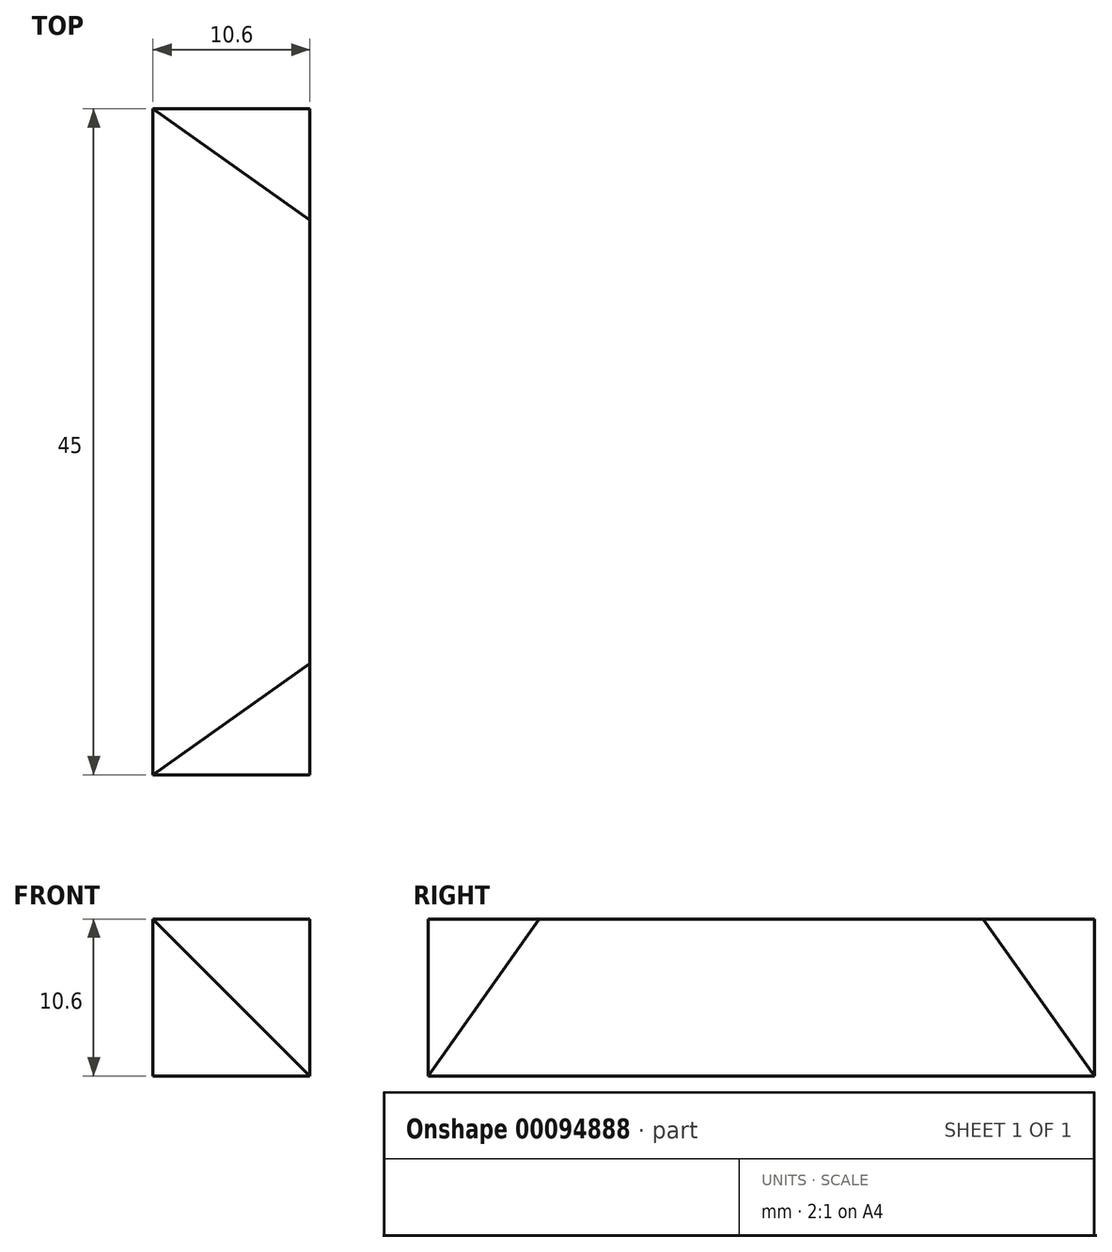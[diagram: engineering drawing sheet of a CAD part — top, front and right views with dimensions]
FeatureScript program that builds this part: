
annotation { "Feature Type Name" : "Feature", "Feature Type Description" : "" }
export const myFeature = defineFeature(function(context is Context, id is Id, definition is map)
    precondition{}
    {
        {
            var Q0;
            Q0=qCreatedBy(makeId("Front.planeOp"),FACE);
            var sketch = newSketch(context, id + "F0", { "sketchPlane" : qUnion([Q0])});
            skLineSegment(sketch, "E0.bottom", {"start": v(5.3, -5.3) * mm, "end": v(-5.3, -5.3) * mm});
            skLineSegment(sketch, "E0.top", {"start": v(5.3, 5.3) * mm, "end": v(-5.3, 5.3) * mm});
            skLineSegment(sketch, "E0.left", {"start": v(5.3, -5.3) * mm, "end": v(5.3, 5.3) * mm});
            skLineSegment(sketch, "E0.right", {"start": v(-5.3, -5.3) * mm, "end": v(-5.3, 5.3) * mm});
            skPoint(sketch, "E0.middle", {"position": v(0, 0) * mm});
            skSolve(sketch);
        }
        {
            var Q0;
            Q0=qSketchRegion(id+"F0",true);
            extrude(context, id + "F1", {"entities" : qUnion([Q0]), "depth" : 45 * mm, "symmetric" : true});
        }
        {
            var Q0;
            Q0=makeQuery(id+"F1.opExtrude","CAP_VERTEX",VERTEX,{"disambiguationData":[OSD([sQuery(id+"F0.wireOp",EDGE,"E0.top"),sQuery(id+"F0.wireOp",EDGE,"E0.left")])],"isStart":false});
            var Q1;
            Q1=makeQuery(id+"F1.opExtrude","CAP_VERTEX",VERTEX,{"disambiguationData":[OSD([sQuery(id+"F0.wireOp",EDGE,"E0.top"),sQuery(id+"F0.wireOp",EDGE,"E0.left")])],"isStart":true});
            var Q2;
            Q2=makeQuery(id+"F1.opExtrude","CAP_VERTEX",VERTEX,{"disambiguationData":[OSD([sQuery(id+"F0.wireOp",EDGE,"E0.bottom"),sQuery(id+"F0.wireOp",EDGE,"E0.right")])],"isStart":true});
            cPlane(context, id + "F2", {"entities" : qUnion([Q0, Q1, Q2]), "cplaneType" : CPlaneType.THREE_POINT, "offset" : 0 * mm, "width" : 150 * mm, "height" : 150 * mm});
        }
        {
            var Q0;
            Q0=qCreatedBy(id+"F2.planeOp",FACE);
            var sketch = newSketch(context, id + "F3", { "sketchPlane" : qUnion([Q0])});
            skLineSegment(sketch, "E1", {"start": v(22.5, 0) * mm, "end": v(15, 7.5) * mm});
            skLineSegment(sketch, "E2", {"start": v(15, -7.5) * mm, "end": v(22.5, 0) * mm});
            skLineSegment(sketch, "E3", {"start": v(15, 7.5) * mm, "end": v(15, 9.5) * mm});
            skLineSegment(sketch, "E4", {"start": v(15, 9.5) * mm, "end": v(24.5, 9.5) * mm});
            skLineSegment(sketch, "E5", {"start": v(24.5, 9.5) * mm, "end": v(24.5, -9.5) * mm});
            skLineSegment(sketch, "E6", {"start": v(24.5, -9.5) * mm, "end": v(15, -9.5) * mm});
            skLineSegment(sketch, "E7", {"start": v(15, -9.5) * mm, "end": v(15, -7.5) * mm});
            skLineSegment(sketch, "E8", {"start": v(0, 16.28) * mm, "end": v(0, -17.75) * mm, "construction": true});
            skLineSegment(sketch, "E9.MirrorCS", {"start": v(-22.5, 0) * mm, "end": v(-15, 7.5) * mm});
            skLineSegment(sketch, "E10.MirrorCS", {"start": v(-15, 7.5) * mm, "end": v(-15, 9.5) * mm});
            skLineSegment(sketch, "E11.MirrorCS", {"start": v(-15, 9.5) * mm, "end": v(-24.5, 9.5) * mm});
            skLineSegment(sketch, "E12.MirrorCS", {"start": v(-24.5, 9.5) * mm, "end": v(-24.5, -9.5) * mm});
            skLineSegment(sketch, "E13.MirrorCS", {"start": v(-24.5, -9.5) * mm, "end": v(-15, -9.5) * mm});
            skLineSegment(sketch, "E14.MirrorCS", {"start": v(-15, -9.5) * mm, "end": v(-15, -7.5) * mm});
            skLineSegment(sketch, "E15.MirrorCS", {"start": v(-15, -7.5) * mm, "end": v(-22.5, 0) * mm});
            skSolve(sketch);
        }
        {
            var Q0;
            Q0=makeQuery(id+"F3.imprint","IMPRINT",FACE,{"disambiguationData":[TD([[makeQuery(id+"F3.imprint","IMPRINT",EDGE,{"derivedFrom":sQuery(id+"F3.wireOp",EDGE,"E9.MirrorCS")}),1.0]])]});
            var Q1;
            Q1=makeQuery(id+"F3.imprint","IMPRINT",FACE,{"disambiguationData":[TD([[makeQuery(id+"F3.imprint","IMPRINT",EDGE,{"derivedFrom":sQuery(id+"F3.wireOp",EDGE,"E1")}),-1.0]])]});
            extrude(context, id + "F4", {"entities" : qUnion([Q0, Q1]), "operationType" : NewBodyOperationType.REMOVE, "oppositeDirection" : true, "depth" : 30 * mm, "symmetric" : true});
        }
    });
